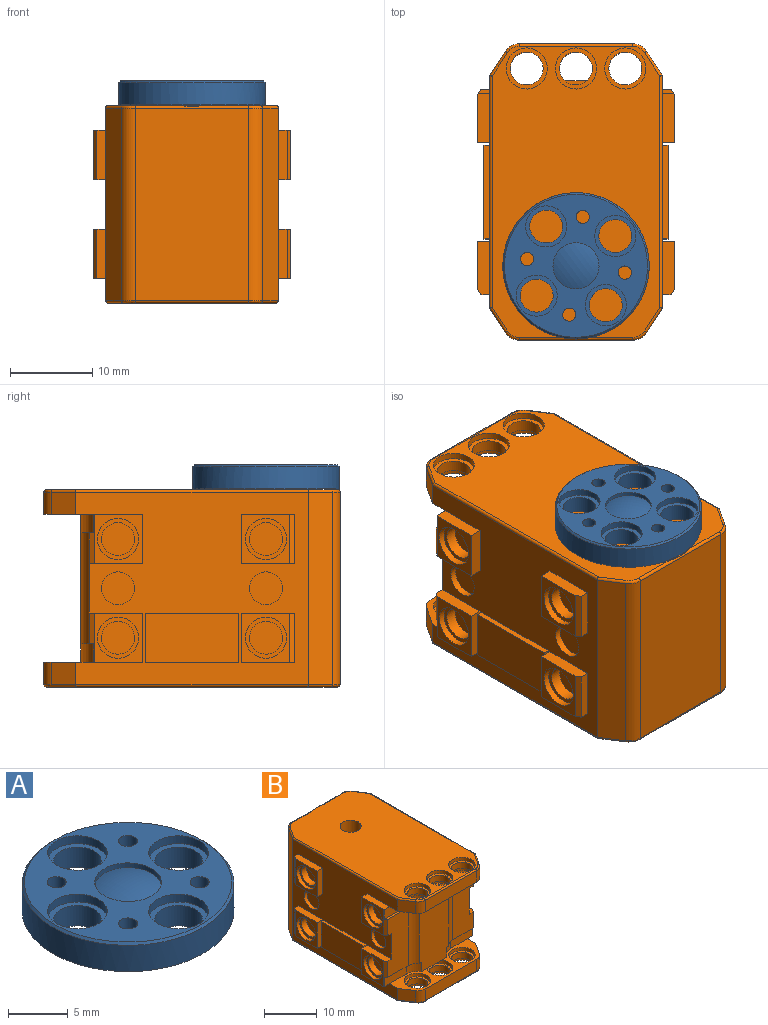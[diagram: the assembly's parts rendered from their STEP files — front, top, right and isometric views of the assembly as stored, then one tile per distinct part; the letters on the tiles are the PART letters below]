
ASSEMBLY  parts=2 mates=1
PART A: 22 faces, bbox 17.8x17.8x2.9 mm
  f0: revolved ~5.62x5.6mm, area 25.4mm2, adj f13
  f1: plane 5x5mm, normal (0,0,1), area 7.1mm2, adj f2,f3
  f2: cylinder r=2mm len=4mm, axis (0,0,1), area 26.4mm2, adj f1,f21
  f3: cylinder r=2.5mm len=5mm, axis (0,0,1), area 12.6mm2, adj f1,f19
  f4: plane 5x5mm, normal (0,0,1), area 7.1mm2, adj f5,f6
  f5: cylinder r=2mm len=4mm, axis (0,0,1), area 26.4mm2, adj f4,f21
  f6: cylinder r=2.5mm len=5mm, axis (0,0,1), area 12.6mm2, adj f4,f19
  f7: plane 5x5mm, normal (0,0,1), area 7.1mm2, adj f8,f9
  f8: cylinder r=2mm len=4mm, axis (0,0,1), area 26.4mm2, adj f7,f21
  f9: cylinder r=2.5mm len=5mm, axis (0,0,1), area 12.6mm2, adj f7,f19
  f10: plane 5x5mm, normal (0,0,1), area 7.1mm2, adj f11,f12
  f11: cylinder r=2mm len=4mm, axis (0,0,1), area 26.4mm2, adj f10,f21
  f12: cylinder r=2.5mm len=5mm, axis (0,0,1), area 12.6mm2, adj f10,f19
  f13: cylinder r=2.8mm len=5.6mm, axis (0,0,1), area 8.8mm2, adj f0,f19
  f14: cone r=8.9mm half-angle=45deg, axis (0,0,-1), area 15.6mm2, adj f15,f19
  f15: cylinder r=8.9mm len=17.8mm, axis (0,0,1), area 151mm2, adj f14,f21
  f16: cylinder r=0.8mm len=2.9mm, axis (0,0,1), area 14.6mm2, adj f19,f21
  f17: cylinder r=0.8mm len=2.9mm, axis (0,0,1), area 14.6mm2, adj f19,f21
  f18: cylinder r=0.8mm len=2.9mm, axis (0,0,1), area 14.6mm2, adj f19,f21
  f19: plane 17.4x17.4mm, normal (0,0,1), area 126.6mm2, adj f3,f6,f9,f12,f13,f14,f16,f17
  f20: cylinder r=0.8mm len=2.9mm, axis (0,0,1), area 14.6mm2, adj f19,f21
  f21: plane 17.8x17.8mm, normal (0,0,-1), area 190.5mm2, adj f2,f5,f8,f11,f15,f16,f17,f18
PART B: 203 faces, bbox 24x36x24 mm
  f0: cylinder r=8.9mm len=3.75mm, axis (0,0,1), area 0mm2, adj f1,f138
  f1: plane 35.6x20.4mm, normal (0,0,1), area 633.5mm2, adj f0,f38,f39,f40,f42,f43,f44,f61
  f2: plane 4x4mm, normal (1,0,0), area 12.6mm2, adj f10
  f3: plane 4x4mm, normal (1,0,0), area 12.6mm2, adj f11
  f4: plane 4x4mm, normal (1,0,0), area 12.6mm2, adj f12
  f5: plane 4x4mm, normal (1,0,0), area 12.6mm2, adj f13
  f6: plane 4x4mm, normal (-1,0,0), area 12.6mm2, adj f14
  f7: plane 4x4mm, normal (-1,0,0), area 12.6mm2, adj f15
  f8: plane 4x4mm, normal (-1,0,0), area 12.6mm2, adj f16
  f9: plane 4x4mm, normal (-1,0,0), area 12.6mm2, adj f17
  f10: cylinder r=2mm len=4mm, axis (1,0,0), area 17.6mm2, adj f2,f18
  f11: cylinder r=2mm len=4mm, axis (1,0,0), area 17.6mm2, adj f3,f19
  f12: cylinder r=2mm len=4mm, axis (1,0,0), area 17.6mm2, adj f4,f20
  f13: cylinder r=2mm len=4mm, axis (1,0,0), area 17.6mm2, adj f5,f21
  f14: cylinder r=2mm len=4mm, axis (1,0,0), area 17.6mm2, adj f6,f28
  f15: cylinder r=2mm len=4mm, axis (1,0,0), area 17.6mm2, adj f7,f29
  f16: cylinder r=2mm len=4mm, axis (1,0,0), area 17.6mm2, adj f8,f31
  f17: cylinder r=2mm len=4mm, axis (1,0,0), area 17.6mm2, adj f9,f32
  f18: plane 5x5mm, normal (1,0,0), area 7.1mm2, adj f10,f34
  f19: plane 5x5mm, normal (1,0,0), area 7.1mm2, adj f11,f35
  f20: plane 5x5mm, normal (1,0,0), area 7.1mm2, adj f12,f36
  f21: plane 5x5mm, normal (1,0,0), area 7.1mm2, adj f13,f37
  f22: plane 5x5mm, normal (0,0,1), area 7.1mm2, adj f26,f38
  f23: plane 5x5mm, normal (0,0,1), area 7.1mm2, adj f25,f39
  f24: plane 5x5mm, normal (0,0,1), area 7.1mm2, adj f27,f40
  f25: cylinder r=2mm len=4mm, axis (0,0,1), area 17.6mm2, adj f23,f41
  f26: cylinder r=2mm len=4mm, axis (0,0,1), area 17.6mm2, adj f22,f45
  f27: cylinder r=2mm len=4mm, axis (0,0,1), area 17.6mm2, adj f24,f46
  f28: plane 5x5mm, normal (-1,0,0), area 7.1mm2, adj f14,f47
  f29: plane 5x5mm, normal (-1,0,0), area 7.1mm2, adj f15,f48
  f30: plane 4x1mm, normal (0,0,1), area 2.8mm2, adj f49,f74
  f31: plane 5x5mm, normal (-1,0,0), area 7.1mm2, adj f16,f50
  f32: plane 5x5mm, normal (-1,0,0), area 7.1mm2, adj f17,f51
  f33: plane 4x1mm, normal (0,0,-1), area 2.8mm2, adj f49,f91
  f34: cylinder r=2.5mm len=5mm, axis (1,0,0), area 12.6mm2, adj f18,f54
  f35: cylinder r=2.5mm len=5mm, axis (1,0,0), area 12.6mm2, adj f19,f60
  f36: cylinder r=2.5mm len=5mm, axis (1,0,0), area 12.6mm2, adj f20,f63
  f37: cylinder r=2.5mm len=5mm, axis (1,0,0), area 12.6mm2, adj f21,f65
  f38: cylinder r=2.5mm len=5mm, axis (0,0,1), area 12.6mm2, adj f1,f22
  f39: cylinder r=2.5mm len=5mm, axis (0,0,1), area 12.6mm2, adj f1,f23
  f40: cylinder r=2.5mm len=5mm, axis (0,0,1), area 12.6mm2, adj f1,f24
  f41: plane 5x5mm, normal (0,0,-1), area 7.1mm2, adj f25,f74
  f42: revolved ~1.68x1.07mm, area 0.9mm2, adj f1,f43,f73,f77
  f43: cylinder r=0.3mm len=13.83mm, axis (1,0,0), area 6.5mm2, adj f1,f42,f44,f78
  f44: revolved ~1.68x1.07mm, area 0.9mm2, adj f1,f43,f61,f79
  f45: plane 5x5mm, normal (0,0,-1), area 7.1mm2, adj f26,f82
  f46: plane 5x5mm, normal (0,0,-1), area 7.1mm2, adj f27,f83
  f47: cylinder r=2.5mm len=5mm, axis (1,0,0), area 12.6mm2, adj f28,f84
  f48: cylinder r=2.5mm len=5mm, axis (1,0,0), area 12.6mm2, adj f29,f90
  f49: plane 18x8mm, normal (0,-1,0), area 138.4mm2, adj f30,f33,f56,f57,f58,f75,f81,f86
  f50: cylinder r=2.5mm len=5mm, axis (1,0,0), area 12.6mm2, adj f31,f99
  f51: cylinder r=2.5mm len=5mm, axis (1,0,0), area 12.6mm2, adj f32,f101
  f52: revolved ~1.68x1.07mm, area 0.9mm2, adj f111,f186,f187,f200
  f53: revolved ~1.68x1.07mm, area 0.9mm2, adj f112,f187,f188,f200
  f54: plane 6x5.84mm, normal (1,0,0), area 15.4mm2, adj f34,f59,f114,f115,f116
  f55: plane 6x0.66mm, normal (0.84,-0.54,0), area 3.3mm2, adj f56,f60,f80,f117,f118,f120
  f56: plane 8.54x1.53mm, normal (0,0,1), area 4.5mm2, adj f49,f55,f57,f80,f81,f117
  f57: cylinder r=2.5mm len=13.5mm, axis (0,0,1), area 31.3mm2, adj f49,f56,f58,f117
  f58: plane 8.54x1.53mm, normal (0,0,-1), area 4.5mm2, adj f49,f57,f59,f94,f95,f117
  f59: plane 6x0.66mm, normal (0.84,-0.54,0), area 3.3mm2, adj f54,f58,f94,f114,f116,f117
  f60: plane 6x5.84mm, normal (1,0,0), area 15.4mm2, adj f35,f55,f118,f119,f120
  f61: cylinder r=0.3mm len=3.1mm, axis (0.54,0.84,0), area 1.6mm2, adj f1,f44,f113,f121
  f62: plane 6x0.66mm, normal (0.84,0.54,0), area 4.7mm2, adj f63,f122,f123,f124
  f63: plane 6x5.84mm, normal (1,0,0), area 15.4mm2, adj f36,f62,f122,f124,f125
  f64: plane 6x0.66mm, normal (0.84,0.54,0), area 4.7mm2, adj f65,f126,f127,f128
  f65: plane 6x5.84mm, normal (1,0,0), area 15.4mm2, adj f37,f64,f126,f128,f129
  f66: plane 4x4mm, normal (1,0,0), area 12.6mm2, adj f130
  f67: plane 4x4mm, normal (1,0,0), area 12.6mm2, adj f131
  f68: plane 11.4x6mm, normal (1,0,0), area 68.4mm2, adj f132,f133,f134,f135
  f69: revolved ~1.68x1.07mm, area 0.9mm2, adj f137,f190,f191,f200
  f70: revolved ~1.68x1.07mm, area 0.9mm2, adj f1,f136,f137,f138
  f71: revolved ~1.68x1.07mm, area 0.9mm2, adj f139,f191,f192,f200
  f72: revolved ~1.68x1.07mm, area 0.9mm2, adj f1,f138,f139,f140
  f73: cylinder r=0.3mm len=3.1mm, axis (0.54,-0.84,0), area 1.6mm2, adj f1,f42,f141,f142
  f74: cylinder r=2.5mm len=5mm, axis (0,0,1), area 12.6mm2, adj f30,f41,f143
  f75: cylinder r=3.02mm len=2.63mm, axis (0,0,1), area 7.2mm2, adj f49,f76,f88,f143
  f76: plane 5.91x2.25mm, normal (0,-1,0), area 13.3mm2, adj f75,f88,f89,f143,f144
  f77: cylinder r=2mm len=2.7mm, axis (0,0,1), area 5.4mm2, adj f42,f78,f142,f143
  f78: plane 13.83x2.7mm, normal (0,-1,0), area 37.3mm2, adj f43,f77,f79,f143
  f79: cylinder r=2mm len=2.7mm, axis (0,0,1), area 5.4mm2, adj f44,f78,f121,f143
  f80: plane 5.91x2.25mm, normal (0,-1,0), area 13.3mm2, adj f55,f56,f81,f120,f143
  f81: cylinder r=3.02mm len=2.63mm, axis (0,0,1), area 7.2mm2, adj f49,f56,f80,f143
  f82: cylinder r=2.5mm len=5mm, axis (0,0,1), area 12.6mm2, adj f45,f143
  f83: cylinder r=2.5mm len=5mm, axis (0,0,1), area 12.6mm2, adj f46,f143
  f84: plane 6x5.84mm, normal (-1,0,0), area 15.4mm2, adj f47,f89,f144,f145,f146
  f85: plane 6x0.66mm, normal (-0.84,-0.54,0), area 3.3mm2, adj f86,f90,f93,f147,f148,f150
  f86: plane 8.54x1.53mm, normal (0,0,-1), area 4.5mm2, adj f49,f85,f87,f92,f93,f147
  f87: cylinder r=2.5mm len=13.5mm, axis (0,0,1), area 31.3mm2, adj f49,f86,f88,f147
  f88: plane 8.54x1.53mm, normal (0,0,1), area 4.5mm2, adj f49,f75,f76,f87,f89,f147
  f89: plane 6x0.66mm, normal (-0.84,-0.54,0), area 3.3mm2, adj f76,f84,f88,f144,f146,f147
  f90: plane 6x5.84mm, normal (-1,0,0), area 15.4mm2, adj f48,f85,f148,f149,f150
  f91: cylinder r=2.5mm len=5mm, axis (0,0,1), area 12.6mm2, adj f33,f109,f151
  f92: cylinder r=3.02mm len=2.63mm, axis (0,0,1), area 7.2mm2, adj f49,f86,f93,f151
  f93: plane 5.91x2.25mm, normal (0,-1,0), area 13.3mm2, adj f85,f86,f92,f150,f151
  f94: plane 5.91x2.25mm, normal (0,-1,0), area 13.3mm2, adj f58,f59,f95,f114,f151
  f95: cylinder r=3.02mm len=2.63mm, axis (0,0,1), area 7.2mm2, adj f49,f58,f94,f151
  f96: cylinder r=2.5mm len=5mm, axis (0,0,1), area 12.6mm2, adj f108,f151
  f97: cylinder r=2.5mm len=5mm, axis (0,0,1), area 12.6mm2, adj f110,f151
  f98: plane 6x0.66mm, normal (-0.84,0.54,0), area 4.7mm2, adj f99,f152,f153,f154
  f99: plane 6x5.84mm, normal (-1,0,0), area 15.4mm2, adj f50,f98,f152,f154,f155
  f100: plane 6x0.66mm, normal (-0.84,0.54,0), area 4.7mm2, adj f101,f156,f157,f158
  f101: plane 6x5.84mm, normal (-1,0,0), area 15.4mm2, adj f51,f100,f156,f158,f159
  f102: plane 4x4mm, normal (-1,0,0), area 12.6mm2, adj f160
  f103: plane 4x4mm, normal (-1,0,0), area 12.6mm2, adj f161
  f104: plane 11.4x6mm, normal (-1,0,0), area 68.4mm2, adj f162,f163,f164,f165
  f105: plane 4x4mm, normal (0,0,-1), area 12.6mm2, adj f166
  f106: plane 4x4mm, normal (0,0,-1), area 12.6mm2, adj f167
  f107: plane 4x4mm, normal (0,0,-1), area 12.6mm2, adj f168
  f108: plane 5x5mm, normal (0,0,1), area 7.1mm2, adj f96,f169
  f109: plane 5x5mm, normal (0,0,1), area 7.1mm2, adj f91,f170
  f110: plane 5x5mm, normal (0,0,1), area 7.1mm2, adj f97,f171
  f111: cylinder r=2mm len=2.7mm, axis (0,0,1), area 5.4mm2, adj f52,f151,f172,f173
  f112: cylinder r=2mm len=2.7mm, axis (0,0,1), area 5.4mm2, adj f53,f151,f173,f174
  f113: cylinder r=0.3mm len=28.3mm, axis (0,1,0), area 13.3mm2, adj f1,f61,f136,f175
  f114: plane 5.98x1.5mm, normal (0,0,-1), area 9mm2, adj f54,f59,f94,f115,f175
  f115: plane 6x1.5mm, normal (0,1,0), area 9mm2, adj f54,f114,f116,f175
  f116: plane 6.5x1.5mm, normal (0,0,1), area 9.6mm2, adj f54,f59,f115,f117,f175
  f117: plane 13.5x5.57mm, normal (0,-1,0), area 68.8mm2, adj f55,f56,f57,f58,f59,f116,f118,f175
  f118: plane 6.5x1.5mm, normal (0,0,-1), area 9.6mm2, adj f55,f60,f117,f119,f175
  f119: plane 6x1.5mm, normal (0,1,0), area 9mm2, adj f60,f118,f120,f175
  f120: plane 5.98x1.5mm, normal (0,0,1), area 9mm2, adj f55,f60,f80,f119,f175
  f121: plane 2.94x2.7mm, normal (0.84,-0.54,0), area 9.5mm2, adj f61,f79,f143,f175
  f122: plane 6.5x1.5mm, normal (0,0,-1), area 9.6mm2, adj f62,f63,f123,f125,f175
  f123: plane 6x1.07mm, normal (0,1,0), area 6.4mm2, adj f62,f122,f124,f175
  f124: plane 6.5x1.5mm, normal (0,0,1), area 9.6mm2, adj f62,f63,f123,f125,f175
  f125: plane 6x1.5mm, normal (0,-1,0), area 9mm2, adj f63,f122,f124,f175
  f126: plane 6.5x1.5mm, normal (0,0,-1), area 9.6mm2, adj f64,f65,f127,f129,f175
  f127: plane 6x1.07mm, normal (0,1,0), area 6.4mm2, adj f64,f126,f128,f175
  f128: plane 6.5x1.5mm, normal (0,0,1), area 9.6mm2, adj f64,f65,f127,f129,f175
  f129: plane 6x1.5mm, normal (0,-1,0), area 9mm2, adj f65,f126,f128,f175
  f130: cylinder r=2mm len=4mm, axis (1,0,0), area 10.1mm2, adj f66,f175
  f131: cylinder r=2mm len=4mm, axis (1,0,0), area 10.1mm2, adj f67,f175
  f132: plane 11.4x0.7mm, normal (0,0,1), area 8mm2, adj f68,f133,f135,f175
  f133: plane 6x0.7mm, normal (0,-1,0), area 4.2mm2, adj f68,f132,f134,f175
  f134: plane 11.4x0.7mm, normal (0,0,-1), area 8mm2, adj f68,f133,f135,f175
  f135: plane 6x0.7mm, normal (0,1,0), area 4.2mm2, adj f68,f132,f134,f175
  f136: cylinder r=0.3mm len=3.1mm, axis (-0.54,0.84,0), area 1.6mm2, adj f1,f70,f113,f176
  f137: cylinder r=2mm len=23.4mm, axis (0,0,-1), area 46.6mm2, adj f69,f70,f176,f177
  f138: cylinder r=0.3mm len=13.83mm, axis (-1,0,0), area 6mm2, adj f0,f1,f70,f72,f177
  f139: cylinder r=2mm len=23.4mm, axis (0,0,-1), area 46.6mm2, adj f71,f72,f177,f178
  f140: cylinder r=0.3mm len=3.1mm, axis (-0.54,-0.84,0), area 1.6mm2, adj f1,f72,f141,f178
  f141: cylinder r=0.3mm len=28.3mm, axis (0,-1,0), area 13.3mm2, adj f1,f73,f140,f179
  f142: plane 2.94x2.7mm, normal (-0.84,-0.54,0), area 9.5mm2, adj f73,f77,f143,f179
  f143: plane 21x6.03mm, normal (0,0,-1), area 47.8mm2, adj f49,f74,f75,f76,f77,f78,f79,f80
  f144: plane 5.98x1.5mm, normal (0,0,1), area 9mm2, adj f76,f84,f89,f145,f179
  f145: plane 6x1.5mm, normal (0,1,0), area 9mm2, adj f84,f144,f146,f179
  f146: plane 6.5x1.5mm, normal (0,0,-1), area 9.6mm2, adj f84,f89,f145,f147,f179
  f147: plane 13.5x5.57mm, normal (0,-1,0), area 68.8mm2, adj f85,f86,f87,f88,f89,f146,f148,f179
  f148: plane 6.5x1.5mm, normal (0,0,1), area 9.6mm2, adj f85,f90,f147,f149,f179
  f149: plane 6x1.5mm, normal (0,1,0), area 9mm2, adj f90,f148,f150,f179
  f150: plane 5.98x1.5mm, normal (0,0,-1), area 9mm2, adj f85,f90,f93,f149,f179
  f151: plane 21x6.03mm, normal (0,0,1), area 47.8mm2, adj f49,f91,f92,f93,f94,f95,f96,f97
  f152: plane 6.5x1.5mm, normal (0,0,1), area 9.6mm2, adj f98,f99,f153,f155,f179
  f153: plane 6x1.07mm, normal (0,1,0), area 6.4mm2, adj f98,f152,f154,f179
  f154: plane 6.5x1.5mm, normal (0,0,-1), area 9.6mm2, adj f98,f99,f153,f155,f179
  f155: plane 6x1.5mm, normal (0,-1,0), area 9mm2, adj f99,f152,f154,f179
  f156: plane 6.5x1.5mm, normal (0,0,1), area 9.6mm2, adj f100,f101,f157,f159,f179
  f157: plane 6x1.07mm, normal (0,1,0), area 6.4mm2, adj f100,f156,f158,f179
  f158: plane 6.5x1.5mm, normal (0,0,-1), area 9.6mm2, adj f100,f101,f157,f159,f179
  f159: plane 6x1.5mm, normal (0,-1,0), area 9mm2, adj f101,f156,f158,f179
  f160: cylinder r=2mm len=4mm, axis (1,0,0), area 10.1mm2, adj f102,f179
  f161: cylinder r=2mm len=4mm, axis (1,0,0), area 10.1mm2, adj f103,f179
  f162: plane 11.4x0.7mm, normal (0,0,1), area 8mm2, adj f104,f163,f165,f179
  f163: plane 6x0.7mm, normal (0,1,0), area 4.2mm2, adj f104,f162,f164,f179
  f164: plane 11.4x0.7mm, normal (0,0,-1), area 8mm2, adj f104,f163,f165,f179
  f165: plane 6x0.7mm, normal (0,-1,0), area 4.2mm2, adj f104,f162,f164,f179
  f166: cylinder r=2mm len=4mm, axis (0,0,-1), area 27.6mm2, adj f105,f180
  f167: cylinder r=2mm len=4mm, axis (0,0,-1), area 27.6mm2, adj f106,f181
  f168: cylinder r=2mm len=4mm, axis (0,0,-1), area 27.6mm2, adj f107,f182
  f169: cylinder r=2mm len=4mm, axis (0,0,1), area 17.6mm2, adj f108,f183
  f170: cylinder r=2mm len=4mm, axis (0,0,1), area 17.6mm2, adj f109,f184
  f171: cylinder r=2mm len=4mm, axis (0,0,1), area 17.6mm2, adj f110,f185
  f172: plane 2.94x2.7mm, normal (-0.84,-0.54,0), area 9.5mm2, adj f111,f151,f179,f186
  f173: plane 13.83x2.7mm, normal (0,-1,0), area 37.3mm2, adj f111,f112,f151,f187
  f174: plane 2.94x2.7mm, normal (0.84,-0.54,0), area 9.5mm2, adj f112,f151,f175,f188
  f175: plane 28.3x23.4mm, normal (1,0,0), area 383mm2, adj f113,f114,f115,f116,f117,f118,f119,f120
  f176: plane 23.4x2.94mm, normal (0.84,0.54,0), area 82mm2, adj f136,f137,f175,f190
  f177: plane 23.4x13.83mm, normal (0,1,0), area 323.6mm2, adj f137,f138,f139,f191
  f178: plane 23.4x2.94mm, normal (-0.84,0.54,0), area 82mm2, adj f139,f140,f179,f192
  f179: plane 28.3x23.4mm, normal (-1,0,0), area 383mm2, adj f141,f142,f143,f144,f145,f146,f147,f148
  f180: plane 5x5mm, normal (0,0,-1), area 7.1mm2, adj f166,f194
  f181: plane 5x5mm, normal (0,0,-1), area 7.1mm2, adj f167,f195
  f182: plane 5x5mm, normal (0,0,-1), area 7.1mm2, adj f168,f196
  f183: plane 5x5mm, normal (0,0,-1), area 7.1mm2, adj f169,f197
  f184: plane 5x5mm, normal (0,0,-1), area 7.1mm2, adj f170,f198
  f185: plane 5x5mm, normal (0,0,-1), area 7.1mm2, adj f171,f199
  f186: cylinder r=0.3mm len=3.1mm, axis (-0.54,0.84,0), area 1.6mm2, adj f52,f172,f193,f200
  f187: cylinder r=0.3mm len=13.83mm, axis (-1,0,0), area 6.5mm2, adj f52,f53,f173,f200
  f188: cylinder r=0.3mm len=3.1mm, axis (-0.54,-0.84,0), area 1.6mm2, adj f53,f174,f189,f200
  f189: cylinder r=0.3mm len=28.3mm, axis (0,-1,0), area 13.3mm2, adj f175,f188,f190,f200
  f190: cylinder r=0.3mm len=3.1mm, axis (0.54,-0.84,0), area 1.6mm2, adj f69,f176,f189,f200
  f191: cylinder r=0.3mm len=13.83mm, axis (1,0,0), area 6.5mm2, adj f69,f71,f177,f200
  f192: cylinder r=0.3mm len=3.1mm, axis (0.54,0.84,0), area 1.6mm2, adj f71,f178,f193,f200
  f193: cylinder r=0.3mm len=28.3mm, axis (0,1,0), area 13.3mm2, adj f179,f186,f192,f200
  f194: cylinder r=2.5mm len=5mm, axis (0,0,-1), area 12.6mm2, adj f180,f200
  f195: cylinder r=2.5mm len=5mm, axis (0,0,-1), area 12.6mm2, adj f181,f200
  f196: cylinder r=2.5mm len=5mm, axis (0,0,-1), area 12.6mm2, adj f182,f200
  f197: cylinder r=2.5mm len=5mm, axis (0,0,-1), area 12.6mm2, adj f183,f200
  f198: cylinder r=2.5mm len=5mm, axis (0,0,-1), area 12.6mm2, adj f184,f200
  f199: cylinder r=2.5mm len=5mm, axis (0,0,-1), area 12.6mm2, adj f185,f200
  f200: plane 35.4x20.4mm, normal (0,0,-1), area 586.6mm2, adj f52,f53,f69,f71,f186,f187,f188,f189
  f201: cylinder r=2mm len=5mm, axis (0,0,1), area 62.8mm2, adj f1,f202
  f202: plane 4x4mm, normal (0,0,1), area 12.6mm2, adj f201
PLACE A rot(axis=(0,0,-1),142.9deg) t=(0,0,12)mm
PLACE B rot(axis=(0,0,1),180deg) t=(0,0,12)mm
MATE revolute A.f13 <-> B.f0  axis (0,0,-1) through (0,0,24)mm
